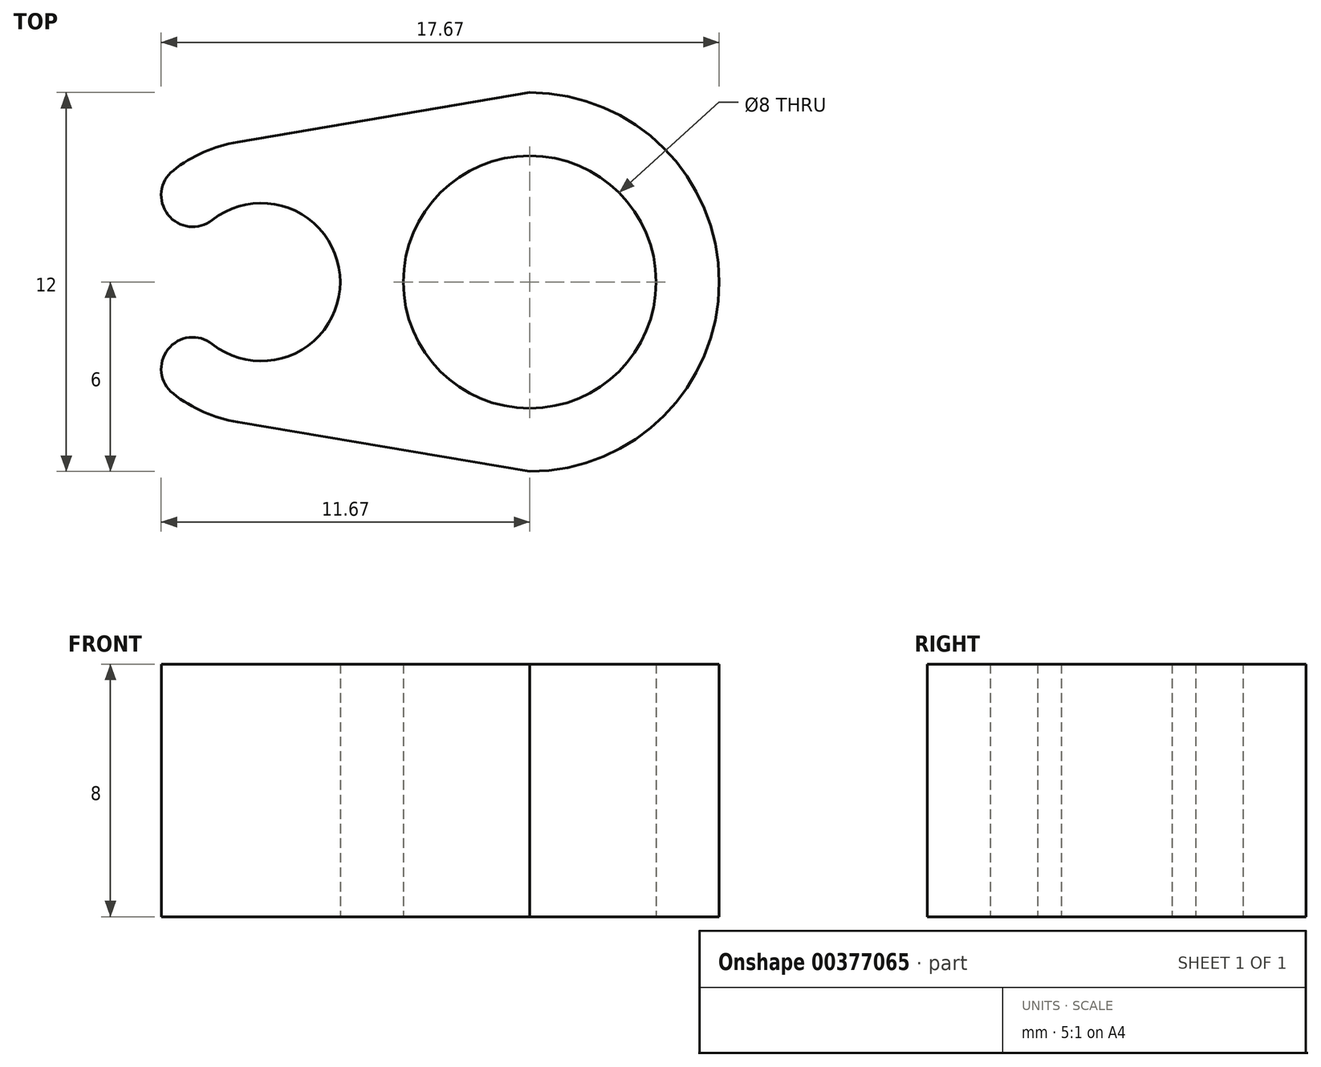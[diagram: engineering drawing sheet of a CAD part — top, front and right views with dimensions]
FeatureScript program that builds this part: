
annotation { "Feature Type Name" : "Feature", "Feature Type Description" : "" }
export const myFeature = defineFeature(function(context is Context, id is Id, definition is map)
    precondition{}
    {
        {
            var Q0;
            Q0=qCreatedBy(makeId("Top.planeOp"),FACE);
            var sketch = newSketch(context, id + "F0", { "sketchPlane" : qUnion([Q0])});
            skCircle(sketch, "E0", {"center": v(0, 0) * mm, "radius": 4 * mm});
            skArc(sketch, "E1.0", {"start": v(0, -6) * mm, "mid": v(6, 0) * mm, "end": v(0, 6) * mm});
            skArc(sketch, "E2", {"start": v(-10.05, -1.96) * mm, "mid": v(-6, 0) * mm, "end": v(-10.05, 1.96) * mm});
            skArc(sketch, "E3.0", {"start": v(-9.25, 4.44) * mm, "mid": v(-10.32, 4.11) * mm, "end": v(-11.28, 3.54) * mm});
            skLineSegment(sketch, "E4", {"start": v(0, 6) * mm, "end": v(-9.25, 4.44) * mm});
            skLineSegment(sketch, "E5", {"start": v(0, -6) * mm, "end": v(-9.25, -4.44) * mm});
            skPoint(sketch, "E6.right.end.orphan", {"position": v(-0.51, 1.75) * mm});
            skPoint(sketch, "E7.orphan", {"position": v(-1.71, -1.27) * mm});
            skArc(sketch, "E8.trimOffspring", {"start": v(-11.28, -3.54) * mm, "mid": v(-10.32, -4.11) * mm, "end": v(-9.25, -4.44) * mm});
            skPoint(sketch, "E9.visualSharp", {"position": v(-10.05, 1.96) * mm});
            skArc(sketch, "E9.filletArc", {"start": v(-11.28, 3.54) * mm, "mid": v(-11.45, 2.13) * mm, "end": v(-10.05, 1.96) * mm});
            skArc(sketch, "E10.filletArc", {"start": v(-10.05, -1.96) * mm, "mid": v(-11.45, -2.13) * mm, "end": v(-11.28, -3.54) * mm});
            skLineSegment(sketch, "E11", {"start": v(-10.67, 2.75) * mm, "end": v(-10.67, -2.75) * mm, "construction": true});
            skSolve(sketch);
        }
        {
            var Q0;
            Q0 = qSketchRegion(id + "F0", true);
            extrude(context, id + "F1", {"entities" : qUnion([Q0]), "depth" : 8 * mm});
        }
    });
